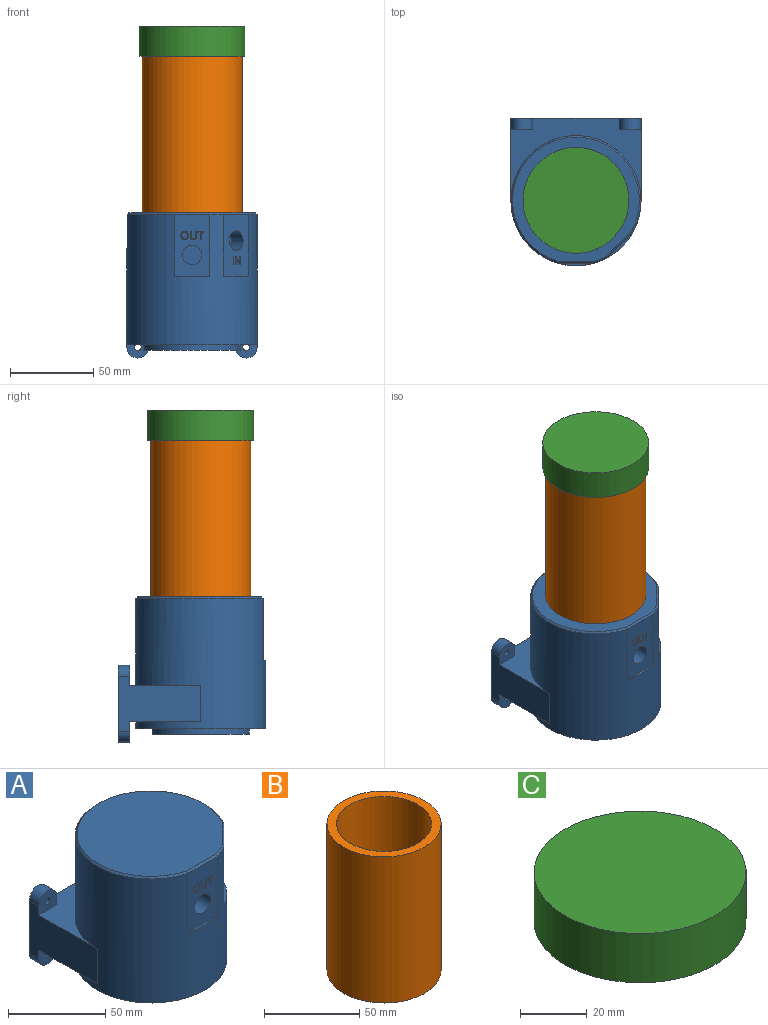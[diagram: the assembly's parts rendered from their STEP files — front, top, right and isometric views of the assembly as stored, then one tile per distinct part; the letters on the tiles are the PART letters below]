
ASSEMBLY  parts=3 mates=2
PART A: 101 faces, bbox 78x88.5x87 mm
  f0: plane 37x15.15mm, normal (0.71,-0.71,0), area 674.2mm2, adj f5,f29,f32,f76,f77,f78,f79,f81
  f1: plane 37x21.42mm, normal (0,-1,0), area 655.2mm2, adj f5,f28,f30,f34,f35,f36,f37,f38
  f2: plane 76x74.5mm, normal (0,0,1), area 4494mm2, adj f97,f98,f99,f100
  f3: plane 78x49.5mm, normal (0,0,1), area 1289.8mm2, adj f5,f6,f7,f8,f9,f12,f19,f20
  f4: plane 78x49.5mm, normal (0,0,-1), area 1289.8mm2, adj f5,f6,f7,f8,f15,f16,f21,f24
  f5: cylinder r=39mm len=78mm, axis (0,0,-1), area 14811.9mm2, adj f0,f1,f3,f4,f6,f8,f25,f28
  f6: plane 49.5x33mm, normal (-1,0,0), area 1166mm2, adj f3,f4,f5,f7,f17,f20,f22,f24
  f7: plane 78x46mm, normal (0,1,0), area 2217.2mm2, adj f3,f4,f6,f8,f9,f10,f11,f13
  f8: plane 49.5x33mm, normal (1,0,0), area 1166mm2, adj f3,f4,f5,f7,f10,f12,f13,f16
  f9: plane 7x5.5mm, normal (-1,0,0), area 38.5mm2, adj f3,f7,f10,f12
  f10: cylinder r=6.5mm len=13mm, axis (0,1,0), area 142.9mm2, adj f7,f8,f9,f12
  f11: cylinder r=2mm len=7mm, axis (0,1,0), area 88mm2, adj f7,f12
  f12: plane 13x12mm, normal (0,-1,0), area 125.3mm2, adj f3,f8,f9,f10,f11
  f13: cylinder r=6.5mm len=13mm, axis (0,1,0), area 142.9mm2, adj f7,f8,f15,f16
  f14: cylinder r=2mm len=7mm, axis (0,1,0), area 88mm2, adj f7,f16
  f15: plane 7x5.5mm, normal (-1,0,0), area 38.5mm2, adj f4,f7,f13,f16
  f16: plane 13x12mm, normal (0,-1,0), area 125.3mm2, adj f4,f8,f13,f14,f15
  f17: cylinder r=6.5mm len=13mm, axis (0,1,0), area 142.9mm2, adj f6,f7,f19,f20
  f18: cylinder r=2mm len=7mm, axis (0,1,0), area 88mm2, adj f7,f20
  f19: plane 7x5.5mm, normal (1,0,0), area 38.5mm2, adj f3,f7,f17,f20
  f20: plane 13x12mm, normal (0,-1,0), area 125.3mm2, adj f3,f6,f17,f18,f19
  f21: plane 7x5.5mm, normal (1,0,0), area 38.5mm2, adj f4,f7,f22,f24
  f22: cylinder r=6.5mm len=13mm, axis (0,1,0), area 142.9mm2, adj f6,f7,f21,f24
  f23: cylinder r=2mm len=7mm, axis (0,1,0), area 88mm2, adj f7,f24
  f24: plane 13x12mm, normal (0,-1,0), area 125.3mm2, adj f4,f6,f21,f22,f23
  f25: plane 78x78mm, normal (0,0,-1), area 2136.3mm2, adj f5,f26
  f26: cylinder r=29mm len=58mm, axis (0,0,1), area 637.7mm2, adj f25,f27
  f27: plane 58x58mm, normal (0,0,-1), area 2642.1mm2, adj f26
  f28: plane 21.42x1.5mm, normal (0,0,1), area 21.5mm2, adj f1,f5
  f29: plane 15.15x15.15mm, normal (0,0,1), area 21.5mm2, adj f0,f5
  f30: cylinder r=5.85mm len=11.7mm, axis (0,-1,0), area 367.6mm2, adj f1,f31
  f31: plane 11.7x11.7mm, normal (0,-1,0), area 107.5mm2, adj f30
  f32: cylinder r=5.85mm len=15.34mm, axis (0.71,-0.71,0), area 367.6mm2, adj f0,f33
  f33: plane 11.7x8.27mm, normal (0.71,-0.71,0), area 107.5mm2, adj f32
  f34: plane 3.21x0.5mm, normal (-1,0,0), area 1.6mm2, adj f1,f35,f47,f48
  f35: plane 0.58x0.5mm, normal (0,0,-1), area 0.3mm2, adj f1,f34,f36,f48
  f36: plane 3.23x0.5mm, normal (1,0,0), area 1.6mm2, adj f1,f35,f37,f48
  f37: extruded ~0.96x0.5mm, area 0.5mm2, adj f1,f36,f38,f48
  f38: extruded ~0.97x0.5mm, area 0.5mm2, adj f1,f37,f39,f48
  f39: extruded ~1x0.5mm, area 0.5mm2, adj f1,f38,f40,f48
  f40: extruded ~0.95x0.5mm, area 0.5mm2, adj f1,f39,f41,f48
  f41: plane 3.23x0.5mm, normal (-1,0,0), area 1.6mm2, adj f1,f40,f42,f48
  f42: plane 0.58x0.5mm, normal (0,0,-1), area 0.3mm2, adj f1,f41,f43,f48
  f43: plane 3.19x0.5mm, normal (1,0,0), area 1.6mm2, adj f1,f42,f44,f48
  f44: extruded ~1.34x0.5mm, area 0.7mm2, adj f1,f43,f45,f48
  f45: extruded ~1.39x0.5mm, area 0.8mm2, adj f1,f44,f46,f48
  f46: extruded ~1.41x0.5mm, area 0.8mm2, adj f1,f45,f47,f48
  f47: extruded ~1.33x0.51mm, area 0.7mm2, adj f1,f34,f46,f48
  f48: plane 5.03x3.79mm, normal (0,-1,0), area 6.5mm2, adj f34,f35,f36,f37,f38,f39,f40,f41
  f49: extruded ~1.53x0.5mm, area 0.8mm2, adj f50,f64,f65,f75
  f50: extruded ~1.51x0.5mm, area 0.8mm2, adj f49,f51,f65,f75
  f51: extruded ~1.25x0.52mm, area 0.7mm2, adj f50,f52,f65,f75
  f52: extruded ~1.24x0.52mm, area 0.7mm2, adj f51,f53,f65,f75
  f53: extruded ~1.52x0.5mm, area 0.8mm2, adj f52,f54,f65,f75
  f54: extruded ~1.53x0.5mm, area 0.8mm2, adj f53,f55,f65,f75
  f55: extruded ~1.24x0.52mm, area 0.7mm2, adj f54,f64,f65,f75
  f56: extruded ~1.87x0.6mm, area 1mm2, adj f1,f57,f63,f65
  f57: extruded ~1.87x0.6mm, area 1mm2, adj f1,f56,f58,f65
  f58: extruded ~1.67x0.68mm, area 0.9mm2, adj f1,f57,f59,f65
  f59: extruded ~1.7x0.67mm, area 0.9mm2, adj f1,f58,f60,f65
  f60: extruded ~1.88x0.6mm, area 1mm2, adj f1,f59,f61,f65
  f61: extruded ~1.89x0.6mm, area 1mm2, adj f1,f60,f62,f65
  f62: extruded ~1.69x0.67mm, area 0.9mm2, adj f1,f61,f63,f65
  f63: extruded ~1.67x0.68mm, area 0.9mm2, adj f1,f56,f62,f65
  f64: extruded ~1.25x0.52mm, area 0.7mm2, adj f49,f55,f65,f75
  f65: plane 5.1x4.56mm, normal (0,-1,0), area 7.8mm2, adj f49,f50,f51,f52,f53,f54,f55,f56
  f66: plane 0.58x0.5mm, normal (0,0,1), area 0.3mm2, adj f1,f67,f73,f74
  f67: plane 4.45x0.5mm, normal (-1,0,0), area 2.2mm2, adj f1,f66,f68,f74
  f68: plane 1.57x0.5mm, normal (0,0,1), area 0.8mm2, adj f1,f67,f69,f74
  f69: plane 0.51x0.5mm, normal (-1,0,0), area 0.3mm2, adj f1,f68,f70,f74
  f70: plane 3.72x0.5mm, normal (0,0,-1), area 1.9mm2, adj f1,f69,f71,f74
  f71: plane 0.51x0.5mm, normal (1,0,0), area 0.3mm2, adj f1,f70,f72,f74
  f72: plane 1.57x0.5mm, normal (0,0,1), area 0.8mm2, adj f1,f71,f73,f74
  f73: plane 4.45x0.5mm, normal (1,0,0), area 2.2mm2, adj f1,f66,f72,f74
  f74: plane 4.96x3.72mm, normal (0,-1,0), area 4.5mm2, adj f66,f67,f68,f69,f70,f71,f72,f73
  f75: plane 4.08x3.34mm, normal (0,-1,0), area 11.3mm2, adj f49,f50,f51,f52,f53,f54,f55,f64
  f76: plane 4.96x0.35mm, normal (0.71,0.71,0), area 2.5mm2, adj f0,f77,f79,f80
  f77: plane 0.76x0.76mm, normal (0,0,1), area 0.3mm2, adj f0,f76,f78,f80
  f78: plane 4.96x0.35mm, normal (-0.71,-0.71,0), area 2.5mm2, adj f0,f77,f79,f80
  f79: plane 0.76x0.76mm, normal (0,0,-1), area 0.3mm2, adj f0,f76,f78,f80
  f80: plane 4.96x0.41mm, normal (0.71,-0.71,0), area 2.9mm2, adj f76,f77,f78,f79
  f81: plane 0.82x0.82mm, normal (0,0,1), area 0.3mm2, adj f0,f82,f95,f96
  f82: plane 4.96x0.35mm, normal (-0.71,-0.71,0), area 2.5mm2, adj f0,f81,f83,f96
  f83: plane 0.74x0.74mm, normal (0,0,-1), area 0.3mm2, adj f0,f82,f84,f96
  f84: plane 2.85x0.35mm, normal (0.71,0.71,0), area 1.4mm2, adj f0,f83,f85,f96
  f85: extruded ~0.71x0.37mm, area 0.4mm2, adj f0,f84,f86,f96
  f86: extruded ~0.59x0.38mm, area 0.3mm2, adj f0,f85,f87,f96
  f87: plane 0.37x0.37mm, normal (0,0,-1), area 0mm2, adj f0,f86,f88,f96
  f88: plane 4.14x2.26mm, normal (-0.59,-0.59,-0.55), area 2.5mm2, adj f0,f87,f89,f96
  f89: plane 0.81x0.81mm, normal (0,0,-1), area 0.3mm2, adj f0,f88,f90,f96
  f90: plane 4.96x0.35mm, normal (0.71,0.71,0), area 2.5mm2, adj f0,f89,f91,f96
  f91: plane 0.73x0.73mm, normal (0,0,1), area 0.3mm2, adj f0,f90,f92,f96
  f92: plane 2.82x0.35mm, normal (-0.71,-0.71,0), area 1.4mm2, adj f0,f91,f93,f96
  f93: extruded ~1.34x0.39mm, area 0.7mm2, adj f0,f92,f94,f96
  f94: plane 0.37x0.37mm, normal (0,0,1), area 0mm2, adj f0,f93,f95,f96
  f95: plane 4.16x2.27mm, normal (0.59,0.59,0.55), area 2.5mm2, adj f0,f81,f94,f96
  f96: plane 4.96x2.74mm, normal (0.71,-0.71,0), area 8.1mm2, adj f81,f82,f83,f84,f85,f86,f87,f88
  f97: plane 21.43x1mm, normal (0,-0.71,0.71), area 30.1mm2, adj f1,f2,f98,f99
  f98: cone r=38mm half-angle=45deg, axis (0,0,-1), area 12.3mm2, adj f2,f5,f97,f100
  f99: cone r=38mm half-angle=45deg, axis (0,0,-1), area 268.8mm2, adj f2,f5,f97,f100
  f100: plane 15.76x15.76mm, normal (0.5,-0.5,0.71), area 30.1mm2, adj f0,f2,f98,f99
PART B: 4 faces, bbox 60x60x94 mm
  f0: cylinder r=25mm len=94mm, axis (0,0,-1), area 14765.5mm2, adj f2,f3
  f1: cylinder r=30mm len=94mm, axis (0,0,-1), area 17718.6mm2, adj f2,f3
  f2: plane 60x60mm, normal (0,0,1), area 863.9mm2, adj f0,f1
  f3: plane 60x60mm, normal (0,0,-1), area 863.9mm2, adj f0,f1
PART C: 3 faces, bbox 63.5x63.5x18 mm
  f0: cylinder r=31.75mm len=63.5mm, axis (0,0,-1), area 3590.8mm2, adj f1,f2
  f1: plane 63.5x63.5mm, normal (0,0,1), area 3166.9mm2, adj f0
  f2: plane 63.5x63.5mm, normal (0,0,-1), area 3166.9mm2, adj f0
PLACE A t=(0,0,7.5)mm
PLACE B t=(0,0,7.5)mm
PLACE C t=(0,0,47.5)mm
MATE fastened B.f0 <-> A.f5  axis (0,0,-1) through (0,0,82.5)mm
MATE fastened C.f0 <-> B.f0  axis (0,0,-1) through (0,0,176.5)mm
